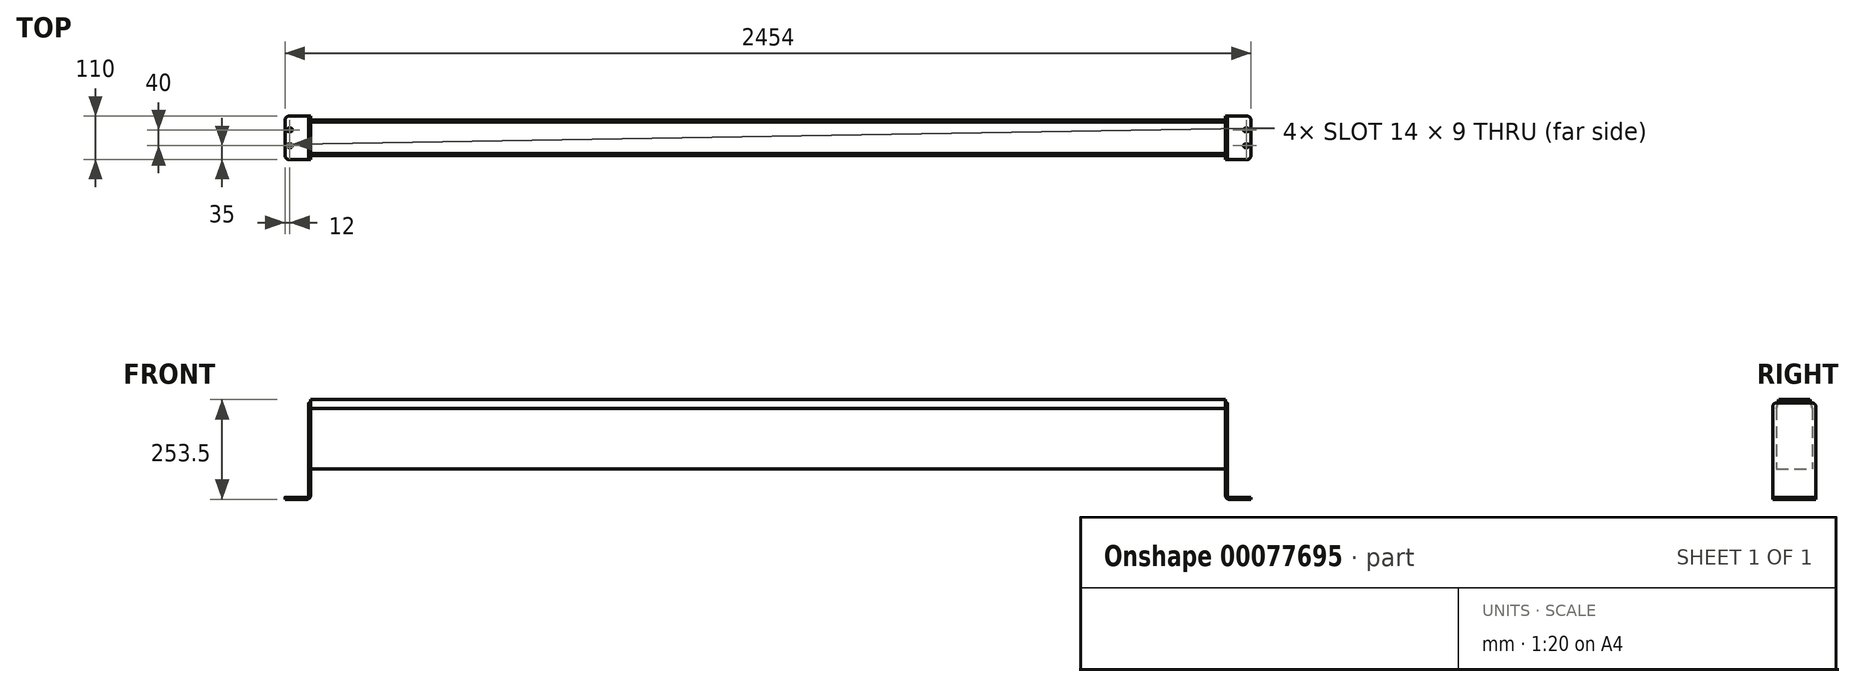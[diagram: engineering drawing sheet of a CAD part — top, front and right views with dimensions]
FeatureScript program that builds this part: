
annotation { "Feature Type Name" : "Feature", "Feature Type Description" : "" }
export const myFeature = defineFeature(function(context is Context, id is Id, definition is map)
    precondition{}
    {
        {
            var Q0;
            Q0=qCreatedBy(makeId("Right.planeOp"),FACE);
            var sketch = newSketch(context, id + "F0", { "sketchPlane" : qUnion([Q0])});
            skLineSegment(sketch, "E0.bottom", {"start": v(-45.5, 88.25) * mm, "end": v(45.5, 88.25) * mm});
            skLineSegment(sketch, "E0.top", {"start": v(-45.5, -88.25) * mm, "end": v(45.5, -88.25) * mm});
            skLineSegment(sketch, "E0.left", {"start": v(-45.5, 88.25) * mm, "end": v(-45.5, -88.25) * mm});
            skLineSegment(sketch, "E0.right", {"start": v(45.5, 88.25) * mm, "end": v(45.5, -88.25) * mm});
            skPoint(sketch, "E0.middle", {"position": v(0, 0) * mm});
            skSolve(sketch);
        }
        {
            var Q0;
            Q0 = qSketchRegion(id + "F0", true);
            extrude(context, id + "F1", {"entities" : qUnion([Q0]), "endBound" : BoundingType.SYMMETRIC, "depth" : 2324 * mm});
        }
        {
            var Q0;
            Q0=makeQuery(id+"F1.opExtrude","SWEPT_EDGE",EDGE,{"disambiguationData":[OSD([sQuery(id+"F0.wireOp",EDGE,"E0.bottom"),sQuery(id+"F0.wireOp",EDGE,"E0.right")])]});
            var Q1;
            Q1=makeQuery(id+"F1.opExtrude","SWEPT_EDGE",EDGE,{"disambiguationData":[OSD([sQuery(id+"F0.wireOp",EDGE,"E0.bottom"),sQuery(id+"F0.wireOp",EDGE,"E0.left")])]});
            chamfer(context, id + "F2", {"entities" : qUnion([Q0, Q1]), "chamferType" : ChamferType.TWO_OFFSETS, "width1" : 6 * mm, "oppositeDirection" : false, "width2" : 22 * mm, "tangentPropagation" : true});
        }
        {
            var Q0;
            Q0=qCreatedBy(makeId("Front.planeOp"),FACE);
            var sketch = newSketch(context, id + "F3", { "sketchPlane" : qUnion([Q0])});
            skLineSegment(sketch, "E1.0", {"start": v(1162, 66.25) * mm, "end": v(1162, -88.25) * mm});
            skLineSegment(sketch, "E2.0", {"start": v(1162, 66.25) * mm, "end": v(1162, 88.25) * mm});
            skLineSegment(sketch, "E3", {"start": v(1162, 88.25) * mm, "end": v(1473.37, 88.25) * mm, "construction": true});
            skLineSegment(sketch, "E4.0", {"start": v(1162, 79.75) * mm, "end": v(1473.37, 79.75) * mm, "construction": true});
            skLineSegment(sketch, "E5.0", {"start": v(1162, -165.25) * mm, "end": v(1473.37, -165.25) * mm, "construction": true});
            skLineSegment(sketch, "E6.0", {"start": v(1162, -160.25) * mm, "end": v(1473.37, -160.25) * mm, "construction": true});
            skLineSegment(sketch, "E7.0", {"start": v(1167, 79.75) * mm, "end": v(1167, -88.25) * mm, "construction": true});
            skLineSegment(sketch, "E8.0", {"start": v(1227, 66.25) * mm, "end": v(1227, -165.25) * mm, "construction": true});
            skLineSegment(sketch, "E9.bottom", {"start": v(1162, 79.75) * mm, "end": v(1167, 79.75) * mm});
            skLineSegment(sketch, "E9.top", {"start": v(1162, -165.25) * mm, "end": v(1167, -165.25) * mm});
            skLineSegment(sketch, "E9.left", {"start": v(1162, 79.75) * mm, "end": v(1162, -155.25) * mm});
            skLineSegment(sketch, "E9.right", {"start": v(1167, 79.75) * mm, "end": v(1167, -155.25) * mm});
            skLineSegment(sketch, "E10.bottom", {"start": v(1227, -165.25) * mm, "end": v(1172, -165.25) * mm});
            skLineSegment(sketch, "E10.top", {"start": v(1227, -160.25) * mm, "end": v(1172, -160.25) * mm});
            skLineSegment(sketch, "E10.left", {"start": v(1227, -165.25) * mm, "end": v(1227, -160.25) * mm});
            skLineSegment(sketch, "E10.right", {"start": v(1162, -165.25) * mm, "end": v(1162, -160.25) * mm});
            skArc(sketch, "E11.filletArc", {"start": v(1167, -155.25) * mm, "mid": v(1168.46, -158.79) * mm, "end": v(1172, -160.25) * mm});
            skPoint(sketch, "E12.visualSharp", {"position": v(1162, -165.25) * mm});
            skArc(sketch, "E12.filletArc", {"start": v(1162, -155.25) * mm, "mid": v(1164.93, -162.32) * mm, "end": v(1172, -165.25) * mm});
            skSolve(sketch);
        }
        {
            var Q0;
            Q0 = qSketchRegion(id + "F3", true);
            extrude(context, id + "F4", {"entities" : qUnion([Q0]), "endBound" : BoundingType.SYMMETRIC, "depth" : 110 * mm});
        }
        {
            var Q0;
            Q0=makeQuery(id+"F4.opExtrude","CAP_EDGE",EDGE,{"disambiguationData":[OSD([sQuery(id+"F3.wireOp",EDGE,"E9.bottom")])],"isStart":true});
            var Q1;
            Q1=makeQuery(id+"F4.opExtrude","CAP_EDGE",EDGE,{"disambiguationData":[OSD([sQuery(id+"F3.wireOp",EDGE,"E9.bottom")])],"isStart":false});
            fillet(context, id + "F5", {"entities" : qUnion([Q0, Q1]), "radius" : 10 * mm, "tangentPropagation" : true, "allowEdgeOverflow" : false});
        }
        {
            var Q0;
            Q0=makeQuery(id+"F4.opExtrude","CAP_EDGE",EDGE,{"disambiguationData":[OSD([sQuery(id+"F3.wireOp",EDGE,"E10.left")])],"isStart":true});
            var Q1;
            Q1=makeQuery(id+"F4.opExtrude","CAP_EDGE",EDGE,{"disambiguationData":[OSD([sQuery(id+"F3.wireOp",EDGE,"E10.left")])],"isStart":false});
            fillet(context, id + "F6", {"entities" : qUnion([Q0, Q1]), "radius" : 10 * mm, "tangentPropagation" : true, "allowEdgeOverflow" : false});
        }
        {
            var Q0;
            Q0=makeQuery(id+"F4.opExtrude","SWEPT_FACE",FACE,{"disambiguationData":[OSD([sQuery(id+"F3.wireOp",EDGE,"E10.bottom")])]});
            var sketch = newSketch(context, id + "F7", { "sketchPlane" : qUnion([Q0])});
            skLineSegment(sketch, "E13", {"start": v(1215, -64.28) * mm, "end": v(1215, 65.9) * mm, "construction": true});
            skLineSegment(sketch, "E14", {"start": v(1161.74, 0) * mm, "end": v(1262.7, 0) * mm, "construction": true});
            skPoint(sketch, "E14.endSnap0", {"position": v(1172, 0) * mm});
            skLineSegment(sketch, "E15.0", {"start": v(1161.74, -20) * mm, "end": v(1262.7, -20) * mm, "construction": true});
            skLineSegment(sketch, "E16.0", {"start": v(1217.5, -64.28) * mm, "end": v(1217.5, 65.9) * mm, "construction": true});
            skLineSegment(sketch, "E17.0", {"start": v(1212.5, -64.28) * mm, "end": v(1212.5, 65.9) * mm, "construction": true});
            skLineSegment(sketch, "E18", {"start": v(1217.5, -20) * mm, "end": v(1212.5, -20) * mm});
            skArc(sketch, "E19.0.startCap", {"start": v(1217.5, -15.5) * mm, "mid": v(1222, -20) * mm, "end": v(1217.5, -24.5) * mm});
            skArc(sketch, "E19.0.endCap", {"start": v(1212.5, -24.5) * mm, "mid": v(1208, -20) * mm, "end": v(1212.5, -15.5) * mm});
            skLineSegment(sketch, "E19.0.left", {"start": v(1217.5, -24.5) * mm, "end": v(1212.5, -24.5) * mm});
            skLineSegment(sketch, "E19.0.right", {"start": v(1217.5, -15.5) * mm, "end": v(1212.5, -15.5) * mm});
            skArc(sketch, "E20.MirrorCS", {"start": v(1217.5, 15.5) * mm, "mid": v(1222, 20) * mm, "end": v(1217.5, 24.5) * mm});
            skLineSegment(sketch, "E21.MirrorCS", {"start": v(1217.5, 20) * mm, "end": v(1212.5, 20) * mm});
            skArc(sketch, "E22.MirrorCS", {"start": v(1212.5, 24.5) * mm, "mid": v(1208, 20) * mm, "end": v(1212.5, 15.5) * mm});
            skLineSegment(sketch, "E23.MirrorCS", {"start": v(1217.5, 15.5) * mm, "end": v(1212.5, 15.5) * mm});
            skLineSegment(sketch, "E24.MirrorCS", {"start": v(1217.5, 24.5) * mm, "end": v(1212.5, 24.5) * mm});
            skSolve(sketch);
        }
        {
            var Q0;
            Q0 = qSketchRegion(id + "F7", true);
            extrude(context, id + "F8", {"entities" : qUnion([Q0]), "operationType" : NewBodyOperationType.REMOVE, "oppositeDirection" : true, "depth" : 25 * mm});
        }
        {
            var Q0;
            Q0=makeQuery(id+"F4.opExtrude","SWEPT_BODY",BODY,{"disambiguationData":[OSD([sQuery(id+"F3.wireOp",EDGE,"E9.bottom"),sQuery(id+"F3.wireOp",EDGE,"E9.left"),sQuery(id+"F3.wireOp",EDGE,"E9.right"),sQuery(id+"F3.wireOp",EDGE,"E10.bottom"),sQuery(id+"F3.wireOp",EDGE,"E10.top"),sQuery(id+"F3.wireOp",EDGE,"E10.left"),sQuery(id+"F3.wireOp",EDGE,"E11.filletArc"),sQuery(id+"F3.wireOp",EDGE,"E12.filletArc")])]});
            var Q1;
            Q1=qCreatedBy(makeId("Right.planeOp"),FACE);
            mirror(context, id + "F9", {"entities" : qUnion([Q0]), "mirrorPlane" : qUnion([Q1])});
        }
    });
